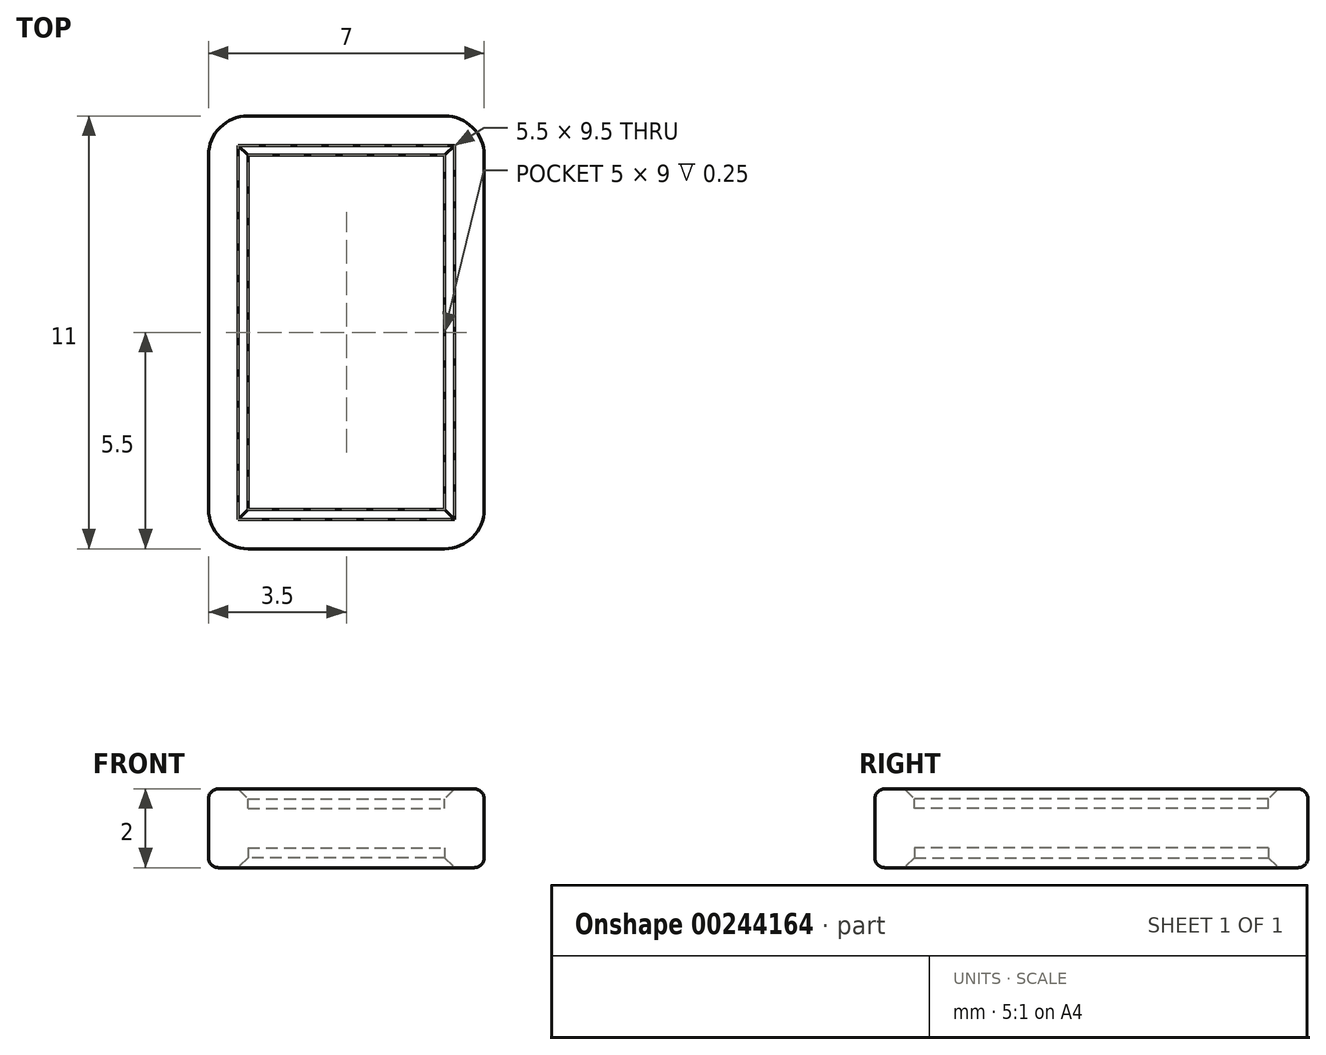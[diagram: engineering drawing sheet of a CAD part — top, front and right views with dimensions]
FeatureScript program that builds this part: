
annotation { "Feature Type Name" : "Feature", "Feature Type Description" : "" }
export const myFeature = defineFeature(function(context is Context, id is Id, definition is map)
    precondition{}
    {
        {
            var Q0;
            Q0=qCreatedBy(makeId("Top.planeOp"),FACE);
            var sketch = newSketch(context, id + "F0", { "sketchPlane" : qUnion([Q0])});
            skLineSegment(sketch, "E0.bottom", {"start": v(0, 0) * mm, "end": v(6, 0) * mm});
            skLineSegment(sketch, "E0.top", {"start": v(0, 10) * mm, "end": v(6, 10) * mm});
            skLineSegment(sketch, "E0.left", {"start": v(0, 0) * mm, "end": v(0, 10) * mm});
            skLineSegment(sketch, "E0.right", {"start": v(6, 0) * mm, "end": v(6, 10) * mm});
            skSolve(sketch);
        }
        {
            var Q0;
            Q0=makeQuery(id+"F0.imprint","IMPRINT",FACE,{"disambiguationData":[TD([[makeQuery(id+"F0.imprint","IMPRINT",EDGE,{"derivedFrom":sQuery(id+"F0.wireOp",EDGE,"E0.bottom")}),1.0]])]});
            extrude(context, id + "F1", {"entities" : qUnion([Q0]), "depth" : 1 * mm});
        }
        {
            var Q0;
            Q0=makeQuery(id+"F1.opExtrude","SWEPT_EDGE",EDGE,{"disambiguationData":[OSD([sQuery(id+"F0.wireOp",EDGE,"E0.bottom"),sQuery(id+"F0.wireOp",EDGE,"E0.right")])]});
            var Q1;
            Q1=makeQuery(id+"F1.opExtrude","SWEPT_EDGE",EDGE,{"disambiguationData":[OSD([sQuery(id+"F0.wireOp",EDGE,"E0.top"),sQuery(id+"F0.wireOp",EDGE,"E0.right")])]});
            var Q2;
            Q2=makeQuery(id+"F1.opExtrude","SWEPT_EDGE",EDGE,{"disambiguationData":[OSD([sQuery(id+"F0.wireOp",EDGE,"E0.bottom"),sQuery(id+"F0.wireOp",EDGE,"E0.left")])]});
            var Q3;
            Q3=makeQuery(id+"F1.opExtrude","SWEPT_EDGE",EDGE,{"disambiguationData":[OSD([sQuery(id+"F0.wireOp",EDGE,"E0.top"),sQuery(id+"F0.wireOp",EDGE,"E0.left")])]});
            fillet(context, id + "F2", {"entities" : qUnion([Q0, Q1, Q2, Q3]), "radius" : .5 * mm, "tangentPropagation" : true, "allowEdgeOverflow" : false});
        }
        {
            var Q0;
            Q0=qCreatedBy(makeId("Front.planeOp"),FACE);
            cPlane(context, id + "F3", {"entities" : qUnion([Q0]), "cplaneType" : CPlaneType.OFFSET, "offset" : .5 * mm, "oppositeDirection" : true, "width" : 150 * mm, "height" : 150 * mm});
        }
        {
            var Q0;
            Q0=qCreatedBy(id+"F3.planeOp",FACE);
            var sketch = newSketch(context, id + "F4", { "sketchPlane" : qUnion([Q0])});
            skLineSegment(sketch, "E1.0", {"start": v(6, 0) * mm, "end": v(5.5, 0) * mm});
            skLineSegment(sketch, "E1.1", {"start": v(6, 1) * mm, "end": v(6, 0) * mm});
            skLineSegment(sketch, "E1.2", {"start": v(5.5, 1) * mm, "end": v(6, 1) * mm});
            skLineSegment(sketch, "E2.0", {"start": v(6.5, -0.5) * mm, "end": v(5.5, -0.5) * mm});
            skLineSegment(sketch, "E2.1", {"start": v(6.5, 1.5) * mm, "end": v(6.5, -0.5) * mm});
            skLineSegment(sketch, "E2.2", {"start": v(5.5, 1.5) * mm, "end": v(6.5, 1.5) * mm});
            skLineSegment(sketch, "E3", {"start": v(5.5, 0) * mm, "end": v(5.5, -0.5) * mm});
            skLineSegment(sketch, "E4", {"start": v(5.5, 1) * mm, "end": v(5.5, 1.5) * mm});
            skSolve(sketch);
        }
        {
            var Q0;
            Q0=makeQuery(id+"F1.opExtrude","CAP_FACE",FACE,{"disambiguationData":[OSD([sQuery(id+"F0.wireOp",EDGE,"E0.bottom"),sQuery(id+"F0.wireOp",EDGE,"E0.top"),sQuery(id+"F0.wireOp",EDGE,"E0.left"),sQuery(id+"F0.wireOp",EDGE,"E0.right")])],"isStart":false});
            var sketch = newSketch(context, id + "F5", { "sketchPlane" : qUnion([Q0])});
            skLineSegment(sketch, "E5.0", {"start": v(6, 0.5) * mm, "end": v(6, 9.5) * mm});
            skArc(sketch, "E5.1", {"start": v(5.5, 0) * mm, "mid": v(5.85, 0.15) * mm, "end": v(6, 0.5) * mm});
            skLineSegment(sketch, "E5.2", {"start": v(0.5, 0) * mm, "end": v(5.5, 0) * mm});
            skArc(sketch, "E5.3", {"start": v(0, 0.5) * mm, "mid": v(0.15, 0.15) * mm, "end": v(0.5, 0) * mm});
            skLineSegment(sketch, "E5.4", {"start": v(0, 0.5) * mm, "end": v(0, 9.5) * mm});
            skArc(sketch, "E5.5", {"start": v(0.5, 10) * mm, "mid": v(0.15, 9.85) * mm, "end": v(0, 9.5) * mm});
            skLineSegment(sketch, "E5.6", {"start": v(0.5, 10) * mm, "end": v(5.5, 10) * mm});
            skArc(sketch, "E5.7", {"start": v(6, 9.5) * mm, "mid": v(5.85, 9.85) * mm, "end": v(5.5, 10) * mm});
            skSolve(sketch);
        }
        {
            var Q0;
            Q0 = qSketchRegion(id + "F4", true);
            var Q1;
            Q1=sQuery(id+"F5.wireOp",EDGE,"E5.1");
            var Q2;
            Q2=sQuery(id+"F5.wireOp",EDGE,"E5.2");
            var Q3;
            Q3=sQuery(id+"F5.wireOp",EDGE,"E5.3");
            var Q4;
            Q4=sQuery(id+"F5.wireOp",EDGE,"E5.4");
            var Q5;
            Q5=sQuery(id+"F5.wireOp",EDGE,"E5.5");
            var Q6;
            Q6=sQuery(id+"F5.wireOp",EDGE,"E5.6");
            var Q7;
            Q7=sQuery(id+"F5.wireOp",EDGE,"E5.7");
            var Q8;
            Q8=sQuery(id+"F5.wireOp",EDGE,"E5.0");
            sweep(context, id + "F6", {"operationType" : NewBodyOperationType.ADD, "profiles" : qUnion([Q0]), "path" : qUnion([Q1, Q2, Q3, Q4, Q5, Q6, Q7, Q8])});
        }
        {
            var Q0;
            Q0=makeQuery(id+"F6.opSweep","SWEPT_EDGE",EDGE,{"disambiguationData":[OSD([sQuery(id+"F4.wireOp",EDGE,"E2.1"),sQuery(id+"F4.wireOp",EDGE,"E2.2"),sQuery(id+"F5.wireOp",EDGE,"E5.4")])]});
            var Q1;
            Q1=makeQuery(id+"F6.opSweep","SWEPT_EDGE",EDGE,{"disambiguationData":[OSD([sQuery(id+"F4.wireOp",EDGE,"E2.0"),sQuery(id+"F4.wireOp",EDGE,"E2.1"),sQuery(id+"F5.wireOp",EDGE,"E5.2")])]});
            fillet(context, id + "F7", {"entities" : qUnion([Q0, Q1]), "radius" : .25 * mm, "tangentPropagation" : true, "allowEdgeOverflow" : false});
        }
        {
            var Q0;
            Q0=makeQuery(id+"F6.opSweep","SWEPT_EDGE",EDGE,{"disambiguationData":[OSD([sQuery(id+"F4.wireOp",EDGE,"E2.2"),sQuery(id+"F4.wireOp",EDGE,"E4"),sQuery(id+"F5.wireOp",EDGE,"E5.4")])]});
            var Q1;
            Q1=makeQuery(id+"F6.opSweep","SWEPT_EDGE",EDGE,{"disambiguationData":[OSD([sQuery(id+"F4.wireOp",EDGE,"E2.2"),sQuery(id+"F4.wireOp",EDGE,"E4"),sQuery(id+"F5.wireOp",EDGE,"E5.6")])]});
            var Q2;
            Q2=makeQuery(id+"F6.opSweep","SWEPT_EDGE",EDGE,{"disambiguationData":[OSD([sQuery(id+"F4.wireOp",EDGE,"E2.2"),sQuery(id+"F4.wireOp",EDGE,"E4"),sQuery(id+"F5.wireOp",EDGE,"E5.0")])]});
            var Q3;
            Q3=makeQuery(id+"F6.opSweep","SWEPT_EDGE",EDGE,{"disambiguationData":[OSD([sQuery(id+"F4.wireOp",EDGE,"E2.2"),sQuery(id+"F4.wireOp",EDGE,"E4"),sQuery(id+"F5.wireOp",EDGE,"E5.2")])]});
            var Q4;
            Q4=makeQuery(id+"F6.opSweep","SWEPT_EDGE",EDGE,{"disambiguationData":[OSD([sQuery(id+"F4.wireOp",EDGE,"E2.0"),sQuery(id+"F4.wireOp",EDGE,"E3"),sQuery(id+"F5.wireOp",EDGE,"E5.4")])]});
            var Q5;
            Q5=makeQuery(id+"F6.opSweep","SWEPT_EDGE",EDGE,{"disambiguationData":[OSD([sQuery(id+"F4.wireOp",EDGE,"E2.0"),sQuery(id+"F4.wireOp",EDGE,"E3"),sQuery(id+"F5.wireOp",EDGE,"E5.2")])]});
            var Q6;
            Q6=makeQuery(id+"F6.opSweep","SWEPT_EDGE",EDGE,{"disambiguationData":[OSD([sQuery(id+"F4.wireOp",EDGE,"E2.0"),sQuery(id+"F4.wireOp",EDGE,"E3"),sQuery(id+"F5.wireOp",EDGE,"E5.0")])]});
            var Q7;
            Q7=makeQuery(id+"F6.opSweep","SWEPT_EDGE",EDGE,{"disambiguationData":[OSD([sQuery(id+"F4.wireOp",EDGE,"E2.0"),sQuery(id+"F4.wireOp",EDGE,"E3"),sQuery(id+"F5.wireOp",EDGE,"E5.6")])]});
            chamfer(context, id + "F8", {"entities" : qUnion([Q0, Q1, Q2, Q3, Q4, Q5, Q6, Q7]), "width" : .25 * mm, "tangentPropagation" : true});
        }
    });
